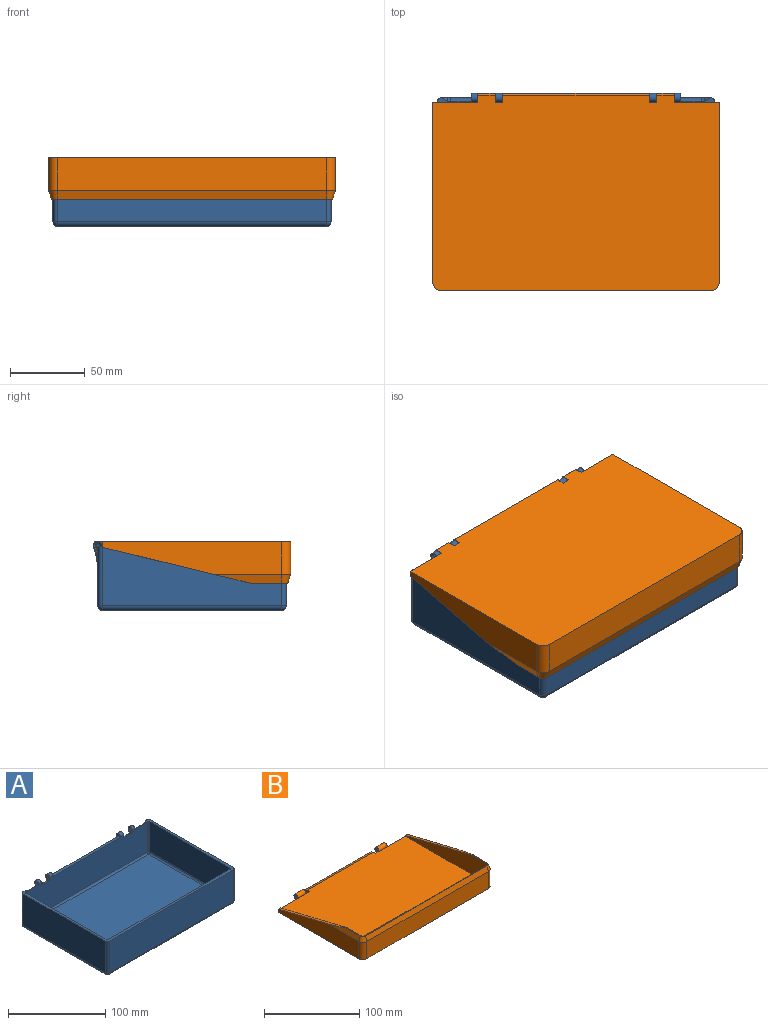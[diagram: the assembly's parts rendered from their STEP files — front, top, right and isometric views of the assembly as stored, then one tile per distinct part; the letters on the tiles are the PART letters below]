
ASSEMBLY  parts=2 mates=1
PART A: 122 faces, bbox 186.6x129.8x46.8 mm
  f0: bspline ~1.89x1.47mm, area 0.5mm2, adj f5,f38,f61
  f1: bspline ~1.89x1.47mm, area 0.5mm2, adj f6,f35,f65
  f2: cylinder r=1.25mm len=3.7mm, axis (1,0,0), area 29.1mm2, adj f32,f34
  f3: plane 180x40mm, normal (0,1,0), area 6546.8mm2, adj f8,f19,f21,f27,f28,f30,f35,f36
  f4: plane 186x126mm, normal (0,0,1), area 1314.4mm2, adj f7,f9,f10,f12,f13,f15,f21,f24
  f5: plane 7.4x6.35mm, normal (1,0,0), area 21.8mm2, adj f0,f22,f29,f38,f50,f51,f52,f61
  f6: plane 7.4x6.35mm, normal (-1,0,0), area 18.7mm2, adj f1,f29,f34,f35,f40,f41,f42,f65
  f7: plane 176x38mm, normal (0,-1,0), area 6613mm2, adj f4,f8,f23,f25,f29,f42,f52,f53
  f8: plane 98.2x4.1mm, normal (0,0,1), area 294.5mm2, adj f3,f7,f26,f36,f45,f83,f93,f102
  f9: plane 120x40mm, normal (-1,0,0), area 4800mm2, adj f4,f15,f18,f21
  f10: plane 180x40mm, normal (0,-1,0), area 7200mm2, adj f4,f15,f16,f74
  f11: plane 180x120mm, normal (0,0,-1), area 21600mm2, adj f16,f18,f19,f76
  f12: plane 176x38mm, normal (0,1,0), area 6688mm2, adj f4,f57,f59,f114
  f13: plane 116x38mm, normal (1,0,0), area 4408mm2, adj f4,f53,f56,f59
  f14: plane 176x116mm, normal (0,0,1), area 20416mm2, adj f54,f56,f57,f112
  f15: cylinder r=3mm len=40mm, axis (0,0,-1), area 188.5mm2, adj f4,f9,f10,f17
  f16: cylinder r=3mm len=180mm, axis (-1,0,0), area 848.2mm2, adj f10,f11,f17,f75
  f17: sphere r=3mm, area 14.1mm2, adj f15,f16,f18
  f18: cylinder r=3mm len=120mm, axis (0,1,0), area 565.5mm2, adj f9,f11,f17,f20
  f19: cylinder r=3mm len=180mm, axis (1,0,0), area 848.2mm2, adj f3,f11,f20,f77
  f20: sphere r=3mm, area 19.3mm2, adj f18,f19,f21
  f21: cylinder r=3mm len=40mm, axis (0,0,1), area 188.5mm2, adj f3,f4,f9,f20,f31
  f22: cylinder r=1.45mm len=2.9mm, axis (1,0,0), area 23.2mm2, adj f5,f33
  f23: cylinder r=3mm len=6mm, axis (1,0,0), area 38.6mm2, adj f7,f28,f48,f51
  f24: plane 6.96x5.91mm, normal (-1,0,0), area 2.1mm2, adj f4,f33,f37,f47,f48
  f25: cylinder r=3mm len=6mm, axis (1,0,0), area 49.1mm2, adj f7,f27,f41,f45
  f26: plane 6.96x5.91mm, normal (1,0,0), area 17.5mm2, adj f8,f36,f44,f45
  f27: cylinder r=50mm len=16.58mm, axis (1,0,0), area 84.5mm2, adj f3,f25,f39,f40,f43,f44
  f28: cylinder r=50mm len=16.58mm, axis (1,0,0), area 67.6mm2, adj f3,f23,f46,f47,f49,f50
  f29: plane 13.83x1.23mm, normal (0,0,1), area 12.6mm2, adj f5,f6,f7,f42,f52,f62,f63,f64
  f30: cylinder r=2.8mm len=13.79mm, axis (1,0,0), area 61.3mm2, adj f3,f4,f33,f37,f66
  f31: plane 0.01x0.01mm, normal (1,0,0), area 0mm2, adj f4,f21,f60
  f32: plane 2.5x2.5mm, normal (-1,0,0), area 4.9mm2, adj f2
  f33: cone r=2.8mm half-angle=45deg, axis (-1,0,0), area 25.5mm2, adj f22,f24,f30
  f34: cone r=1.75mm half-angle=45deg, axis (-1,0,0), area 6.7mm2, adj f2,f6
  f35: cylinder r=1.1mm len=14.68mm, axis (0,0,-1), area 9.3mm2, adj f1,f3,f6,f39,f64,f65
  f36: cylinder r=1.1mm len=17.58mm, axis (0,0,1), area 18.6mm2, adj f3,f8,f26,f43
  f37: cylinder r=1.1mm len=15mm, axis (0,0,-1), area 14mm2, adj f3,f24,f30,f46
  f38: cylinder r=1.1mm len=14.68mm, axis (0,0,1), area 9.3mm2, adj f0,f3,f5,f49,f61,f62
  f39: bspline ~13.63x2.16mm, area 7.4mm2, adj f27,f35,f40
  f40: bspline ~3.19x1.73mm, area 1.8mm2, adj f6,f27,f39,f41
  f41: torus R=2.9mm, axis (1,0,0), area 1.6mm2, adj f6,f25,f40,f42
  f42: bspline ~3.19x0.91mm, area 1.7mm2, adj f6,f7,f29,f41
  f43: bspline ~13.63x2.16mm, area 7.4mm2, adj f27,f36,f44
  f44: bspline ~3.19x1.73mm, area 1.8mm2, adj f26,f27,f43,f45
  f45: torus R=2.9mm, axis (1,0,0), area 1.6mm2, adj f8,f25,f26,f44
  f46: bspline ~13.63x2.16mm, area 7.4mm2, adj f28,f37,f47
  f47: bspline ~3.19x1.73mm, area 1.8mm2, adj f24,f28,f46,f48
  f48: torus R=2.9mm, axis (1,0,0), area 1.6mm2, adj f4,f23,f24,f47
  f49: bspline ~13.63x2.16mm, area 7.4mm2, adj f28,f38,f50
  f50: bspline ~3.19x1.73mm, area 1.8mm2, adj f5,f28,f49,f51
  f51: torus R=2.9mm, axis (1,0,0), area 1.6mm2, adj f5,f23,f50,f52
  f52: bspline ~3.19x0.91mm, area 1.7mm2, adj f5,f7,f29,f51
  f53: cylinder r=2mm len=38mm, axis (0,0,1), area 119.4mm2, adj f4,f7,f13,f55
  f54: cylinder r=2mm len=176mm, axis (1,0,0), area 552.9mm2, adj f7,f14,f55,f111
  f55: sphere r=2mm, area 8.6mm2, adj f53,f54,f56
  f56: cylinder r=2mm len=116mm, axis (0,1,0), area 364.4mm2, adj f13,f14,f55,f58
  f57: cylinder r=2mm len=176mm, axis (-1,0,0), area 552.9mm2, adj f12,f14,f58,f113
  f58: sphere r=2mm, area 6.3mm2, adj f56,f57,f59
  f59: cylinder r=2mm len=38mm, axis (0,0,-1), area 119.4mm2, adj f4,f12,f13,f58
  f60: cone r=2.8mm half-angle=28.2deg, axis (1,0,0), area 9mm2, adj f3,f4,f31,f66
  f61: bspline ~2.39x2mm, area 1.7mm2, adj f0,f5,f38,f62
  f62: torus R=3.1mm, axis (0,0,1), area 2.1mm2, adj f29,f38,f61,f63
  f63: cylinder r=2mm len=10mm, axis (-1,0,0), area 31.4mm2, adj f3,f29,f62,f64
  f64: torus R=3.1mm, axis (0,0,1), area 2.1mm2, adj f29,f35,f63,f65
  f65: bspline ~2.39x2mm, area 1.7mm2, adj f1,f6,f35,f64
  f66: revolved ~2.8x2.8mm, area 8.2mm2, adj f3,f4,f30,f60
  f67: bspline ~1.89x1.47mm, area 0.5mm2, adj f70,f95,f116
  f68: bspline ~1.89x1.47mm, area 0.5mm2, adj f71,f92,f120
  f69: cylinder r=1.25mm len=3.7mm, axis (-1,0,0), area 29.1mm2, adj f89,f91
  f70: plane 7.4x6.35mm, normal (-1,0,0), area 21.8mm2, adj f67,f79,f86,f95,f107,f108,f109,f116
  f71: plane 7.4x6.35mm, normal (1,0,0), area 18.7mm2, adj f68,f86,f91,f92,f97,f98,f99,f120
  f72: plane 120x40mm, normal (1,0,0), area 4800mm2, adj f4,f74,f76,f78
  f73: plane 116x38mm, normal (-1,0,0), area 4408mm2, adj f4,f110,f112,f114
  f74: cylinder r=3mm len=40mm, axis (0,0,-1), area 188.5mm2, adj f4,f10,f72,f75
  f75: sphere r=3mm, area 19.3mm2, adj f16,f74,f76
  f76: cylinder r=3mm len=120mm, axis (0,1,0), area 565.5mm2, adj f11,f72,f75,f77
  f77: sphere r=3mm, area 14.1mm2, adj f19,f76,f78
  f78: cylinder r=3mm len=40mm, axis (0,0,1), area 188.5mm2, adj f3,f4,f72,f77,f88
  f79: cylinder r=1.45mm len=2.9mm, axis (-1,0,0), area 23.2mm2, adj f70,f90
  f80: cylinder r=3mm len=6mm, axis (-1,0,0), area 38.6mm2, adj f7,f85,f105,f108
  f81: plane 6.96x5.91mm, normal (1,0,0), area 2.1mm2, adj f4,f90,f94,f104,f105
  f82: cylinder r=3mm len=6mm, axis (-1,0,0), area 49.1mm2, adj f7,f84,f98,f102
  f83: plane 6.96x5.91mm, normal (-1,0,0), area 17.5mm2, adj f8,f93,f101,f102
  f84: cylinder r=50mm len=16.58mm, axis (-1,0,0), area 84.5mm2, adj f3,f82,f96,f97,f100,f101
  f85: cylinder r=50mm len=16.58mm, axis (-1,0,0), area 67.6mm2, adj f3,f80,f103,f104,f106,f107
  f86: plane 13.83x1.23mm, normal (0,0,1), area 12.6mm2, adj f7,f70,f71,f99,f109,f117,f118,f119
  f87: cylinder r=2.8mm len=13.79mm, axis (-1,0,0), area 61.3mm2, adj f3,f4,f90,f94,f121
  f88: plane 0.01x0.01mm, normal (-1,0,0), area 0mm2, adj f4,f78,f115
  f89: plane 2.5x2.5mm, normal (1,0,0), area 4.9mm2, adj f69
  f90: cone r=2.8mm half-angle=45deg, axis (1,0,0), area 25.5mm2, adj f79,f81,f87
  f91: cone r=1.75mm half-angle=45deg, axis (1,0,0), area 6.7mm2, adj f69,f71
  f92: cylinder r=1.1mm len=14.68mm, axis (0,0,-1), area 9.3mm2, adj f3,f68,f71,f96,f119,f120
  f93: cylinder r=1.1mm len=17.58mm, axis (0,0,1), area 18.6mm2, adj f3,f8,f83,f100
  f94: cylinder r=1.1mm len=15mm, axis (0,0,-1), area 14mm2, adj f3,f81,f87,f103
  f95: cylinder r=1.1mm len=14.68mm, axis (0,0,1), area 9.3mm2, adj f3,f67,f70,f106,f116,f117
  f96: bspline ~13.63x2.16mm, area 7.4mm2, adj f84,f92,f97
  f97: bspline ~3.19x1.73mm, area 1.8mm2, adj f71,f84,f96,f98
  f98: torus R=2.9mm, axis (-1,0,0), area 1.6mm2, adj f71,f82,f97,f99
  f99: bspline ~3.19x0.91mm, area 1.7mm2, adj f7,f71,f86,f98
  f100: bspline ~13.63x2.16mm, area 7.4mm2, adj f84,f93,f101
  f101: bspline ~3.19x1.73mm, area 1.8mm2, adj f83,f84,f100,f102
  f102: torus R=2.9mm, axis (-1,0,0), area 1.6mm2, adj f8,f82,f83,f101
  f103: bspline ~13.63x2.16mm, area 7.4mm2, adj f85,f94,f104
  f104: bspline ~3.19x1.73mm, area 1.8mm2, adj f81,f85,f103,f105
  f105: torus R=2.9mm, axis (-1,0,0), area 1.6mm2, adj f4,f80,f81,f104
  f106: bspline ~13.63x2.16mm, area 7.4mm2, adj f85,f95,f107
  f107: bspline ~3.19x1.73mm, area 1.8mm2, adj f70,f85,f106,f108
  f108: torus R=2.9mm, axis (-1,0,0), area 1.6mm2, adj f70,f80,f107,f109
  f109: bspline ~3.19x0.91mm, area 1.7mm2, adj f7,f70,f86,f108
  f110: cylinder r=2mm len=38mm, axis (0,0,1), area 119.4mm2, adj f4,f7,f73,f111
  f111: sphere r=2mm, area 6.3mm2, adj f54,f110,f112
  f112: cylinder r=2mm len=116mm, axis (0,1,0), area 364.4mm2, adj f14,f73,f111,f113
  f113: sphere r=2mm, area 8.6mm2, adj f57,f112,f114
  f114: cylinder r=2mm len=38mm, axis (0,0,-1), area 119.4mm2, adj f4,f12,f73,f113
  f115: cone r=2.8mm half-angle=28.2deg, axis (-1,0,0), area 9mm2, adj f3,f4,f88,f121
  f116: bspline ~2.39x2mm, area 1.7mm2, adj f67,f70,f95,f117
  f117: torus R=3.1mm, axis (0,0,1), area 2.1mm2, adj f86,f95,f116,f118
  f118: cylinder r=2mm len=10mm, axis (1,0,0), area 31.4mm2, adj f3,f86,f117,f119
  f119: torus R=3.1mm, axis (0,0,1), area 2.1mm2, adj f86,f92,f118,f120
  f120: bspline ~2.39x2mm, area 1.7mm2, adj f68,f71,f92,f119
  f121: revolved ~2.8x2.8mm, area 8.2mm2, adj f3,f4,f87,f115
PART B: 41 faces, bbox 192x132x28 mm
  f0: plane 6.29x3mm, normal (-1,0,0), area 16.8mm2, adj f1,f2,f3,f4,f23,f24
  f1: extruded ~97.8x0.53mm, area 53.3mm2, adj f0,f2,f24,f25
  f2: extruded ~97.8x1.68mm, area 195.3mm2, adj f0,f1,f4,f25
  f3: plane 186x126mm, normal (0,0,1), area 23146mm2, adj f0,f8,f12,f13,f18,f20,f21,f22
  f4: plane 192x130.81mm, normal (0,0,-1), area 24738.7mm2, adj f0,f2,f6,f7,f10,f11,f20,f21
  f5: extruded ~12x1.32mm, area 16mm2, adj f6,f18,f20,f21
  f6: extruded ~12x1.68mm, area 24mm2, adj f4,f5,f20,f21
  f7: plane 180x22mm, normal (0,-1,0), area 3960mm2, adj f4,f11,f15,f29
  f8: plane 180x25mm, normal (0,1,0), area 4500mm2, adj f3,f9,f12,f30
  f9: plane 188x24.34mm, normal (0,0,1), area 231.7mm2, adj f8,f12,f13,f14,f15,f16,f17,f30
  f10: plane 119.67x22mm, normal (-1,0,0), area 1953.5mm2, adj f4,f11,f14,f17,f22
  f11: cylinder r=6mm len=22mm, axis (0,0,1), area 207.3mm2, adj f4,f7,f10,f16
  f12: cylinder r=3mm len=25mm, axis (0,0,-1), area 117.8mm2, adj f3,f8,f9,f13
  f13: plane 119.67x25mm, normal (1,0,0), area 1790.4mm2, adj f3,f9,f12,f14,f22
  f14: plane 99.32x24.19mm, normal (0,0.24,0.97), area 281.3mm2, adj f9,f10,f13,f17,f22
  f15: plane 180x6mm, normal (0,-0.95,0.32), area 1138.4mm2, adj f7,f9,f16,f33
  f16: cone r=4mm half-angle=18.4deg, axis (0,0,-1), area 49.7mm2, adj f9,f11,f15,f17
  f17: plane 44.98x6mm, normal (-0.95,0,0.32), area 206.6mm2, adj f9,f10,f14,f16
  f18: cylinder r=3mm len=12mm, axis (-1,0,0), area 113.1mm2, adj f3,f5,f20,f21
  f19: cylinder r=1.5mm len=12mm, axis (-1,0,0), area 113.1mm2, adj f20,f21
  f20: plane 6.34x6mm, normal (1,0,0), area 25.1mm2, adj f3,f4,f5,f6,f18,f19,f23
  f21: plane 6.34x6mm, normal (-1,0,0), area 25.1mm2, adj f3,f4,f5,f6,f18,f19,f22
  f22: plane 30x3.81mm, normal (0,1,0), area 92.4mm2, adj f3,f4,f10,f13,f14,f21
  f23: plane 5.1x3mm, normal (0,1,0), area 15.3mm2, adj f0,f3,f4,f20
  f24: plane 97.8x2.95mm, normal (0,0.26,0.97), area 298.3mm2, adj f0,f1,f3,f25
  f25: plane 6.29x3mm, normal (1,0,0), area 16.8mm2, adj f1,f2,f3,f4,f24,f40
  f26: extruded ~12x1.32mm, area 16mm2, adj f27,f35,f37,f38
  f27: extruded ~12x1.68mm, area 24mm2, adj f4,f26,f37,f38
  f28: plane 119.67x22mm, normal (1,0,0), area 1953.5mm2, adj f4,f29,f32,f34,f39
  f29: cylinder r=6mm len=22mm, axis (0,0,1), area 207.3mm2, adj f4,f7,f28,f33
  f30: cylinder r=3mm len=25mm, axis (0,0,-1), area 117.8mm2, adj f3,f8,f9,f31
  f31: plane 119.67x25mm, normal (-1,0,0), area 1790.4mm2, adj f3,f9,f30,f32,f39
  f32: plane 99.32x24.19mm, normal (0,0.24,0.97), area 281.3mm2, adj f9,f28,f31,f34,f39
  f33: cone r=4mm half-angle=18.4deg, axis (0,0,-1), area 49.7mm2, adj f9,f15,f29,f34
  f34: plane 44.98x6mm, normal (0.95,0,0.32), area 206.6mm2, adj f9,f28,f32,f33
  f35: cylinder r=3mm len=12mm, axis (1,0,0), area 113.1mm2, adj f3,f26,f37,f38
  f36: cylinder r=1.5mm len=12mm, axis (1,0,0), area 113.1mm2, adj f37,f38
  f37: plane 6.34x6mm, normal (-1,0,0), area 25.1mm2, adj f3,f4,f26,f27,f35,f36,f40
  f38: plane 6.34x6mm, normal (1,0,0), area 25.1mm2, adj f3,f4,f26,f27,f35,f36,f39
  f39: plane 30x3.81mm, normal (0,1,0), area 92.4mm2, adj f3,f4,f28,f31,f32,f38
  f40: plane 5.1x3mm, normal (0,1,0), area 15.3mm2, adj f3,f4,f25,f37
PLACE A t=(0,0,3)mm
PLACE B rot(axis=(0,-1,0),180deg) t=(0,0,43)mm
MATE revolute B.f36 <-> A.f2  axis (1,0,0) through (66,63,43)mm
